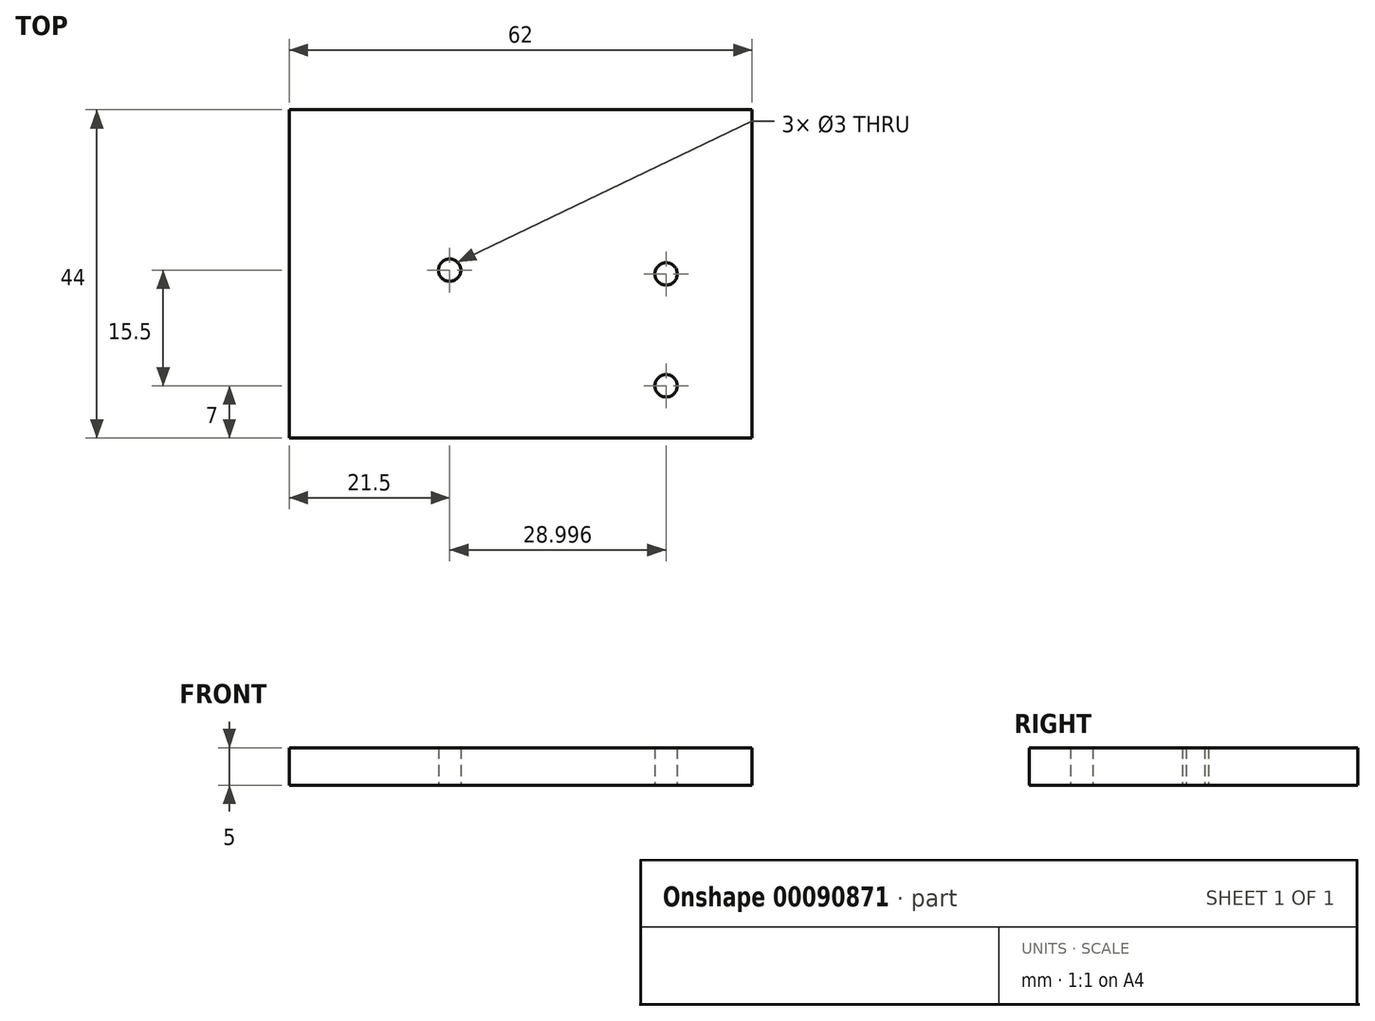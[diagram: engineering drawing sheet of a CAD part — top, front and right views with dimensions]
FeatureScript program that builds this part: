
annotation { "Feature Type Name" : "Feature", "Feature Type Description" : "" }
export const myFeature = defineFeature(function(context is Context, id is Id, definition is map)
    precondition{}
    {
        {
            var Q0;
            Q0=qCreatedBy(makeId("Top.planeOp"),FACE);
            var sketch = newSketch(context, id + "F0", { "sketchPlane" : qUnion([Q0])});
            skLineSegment(sketch, "E0.bottom", {"start": v(31, 22) * mm, "end": v(-31, 22) * mm});
            skLineSegment(sketch, "E0.top", {"start": v(31, -22) * mm, "end": v(-31, -22) * mm});
            skLineSegment(sketch, "E0.left", {"start": v(31, 22) * mm, "end": v(31, -22) * mm});
            skLineSegment(sketch, "E0.right", {"start": v(-31, 22) * mm, "end": v(-31, -22) * mm});
            skPoint(sketch, "E0.middle", {"position": v(0, 0) * mm});
            skLineSegment(sketch, "E1", {"start": v(-31, 22) * mm, "end": v(-31, 0.5) * mm});
            skLineSegment(sketch, "E2", {"start": v(-31, 0.5) * mm, "end": v(-9.5, 0.5) * mm});
            skCircle(sketch, "E3", {"center": v(-9.5, 0.5) * mm, "radius": 1.5 * mm});
            skLineSegment(sketch, "E4", {"start": v(-9.5, 0.5) * mm, "end": v(19.5, 0) * mm});
            skCircle(sketch, "E5", {"center": v(19.5, 0) * mm, "radius": 1.5 * mm});
            skLineSegment(sketch, "E6", {"start": v(19.5, 0) * mm, "end": v(19.5, -15) * mm});
            skCircle(sketch, "E7", {"center": v(19.5, -15) * mm, "radius": 1.5 * mm});
            skSolve(sketch);
        }
        {
            var Q0;
            Q0=makeQuery(id+"F0.imprint","IMPRINT",FACE,{"disambiguationData":[TD([[makeQuery(id+"F0.imprint","IMPRINT",EDGE,{"derivedFrom":sQuery(id+"F0.wireOp",EDGE,"E0.bottom")}),1.0]])]});
            extrude(context, id + "F1", {"entities" : qUnion([Q0]), "depth" : 5 * mm});
        }
    });
